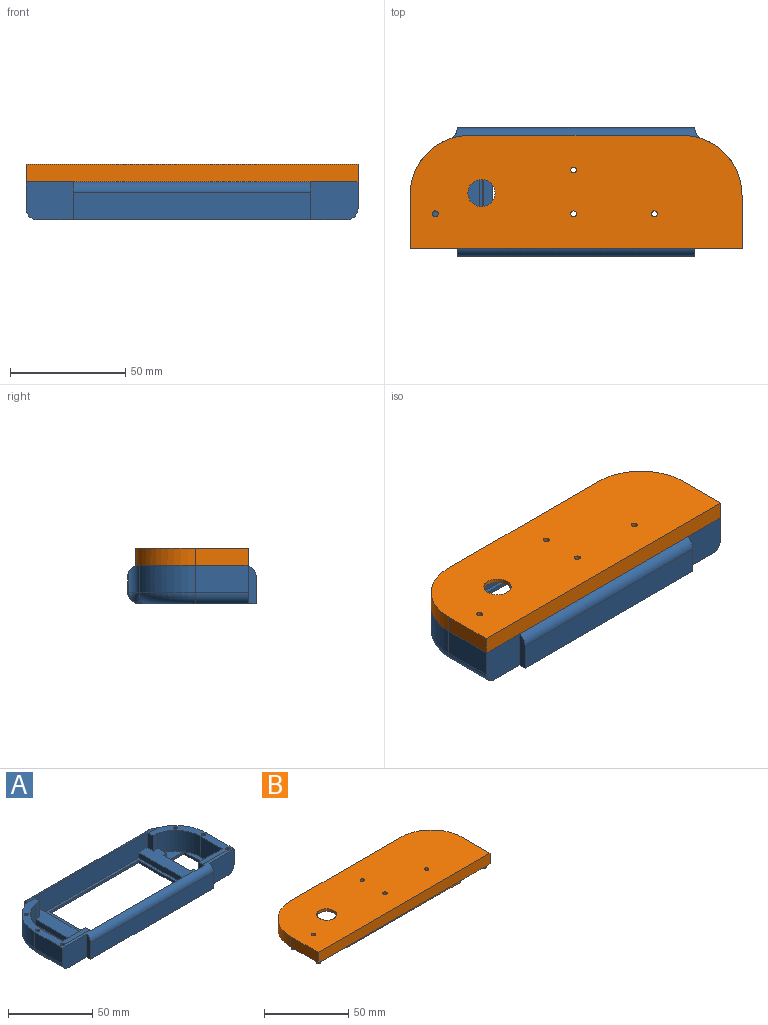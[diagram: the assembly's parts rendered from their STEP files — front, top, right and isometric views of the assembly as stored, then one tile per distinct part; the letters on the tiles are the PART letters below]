
ASSEMBLY  parts=2 mates=1
PART A: 89 faces, bbox 148.3x55.8x16.8 mm
  f0: plane 1.02x0.5mm, normal (0,-1,0), area 0.3mm2, adj f34,f35,f36
  f1: plane 47.75x9.68mm, normal (0,0,1), area 419.8mm2, adj f4,f6,f16,f28,f29,f39,f79,f83
  f2: plane 74.71x1.75mm, normal (0,1,0), area 130.7mm2, adj f12,f42,f43,f80
  f3: plane 74.71x1.75mm, normal (0,-1,0), area 130.7mm2, adj f12,f42,f43,f80
  f4: plane 38.27x4mm, normal (-1,0,0), area 153.1mm2, adj f1,f15,f16,f48
  f5: plane 45.75x24.5mm, normal (0,0,1), area 329.7mm2, adj f6,f15,f16,f17,f22,f23,f39,f55
  f6: plane 11x5.11mm, normal (1,0,0), area 56.2mm2, adj f1,f5,f29,f77,f79
  f7: plane 45.75x24.5mm, normal (0,0,1), area 329.7mm2, adj f14,f18,f19,f20,f41,f44,f45,f49
  f8: plane 8.13x4mm, normal (1,0,0), area 32.5mm2, adj f19,f40,f47,f52
  f9: plane 18.75x1.75mm, normal (1,0,0), area 32.8mm2, adj f10,f11,f12,f47
  f10: plane 13.13x1.75mm, normal (0,-1,0), area 23mm2, adj f9,f12,f47,f50
  f11: plane 13.13x1.75mm, normal (0,1,0), area 23mm2, adj f9,f12,f47,f50
  f12: plane 134x50.75mm, normal (0,0,-1), area 2811.7mm2, adj f2,f3,f9,f10,f11,f21,f24,f26
  f13: plane 7.39x4mm, normal (1,0,0), area 29.6mm2, adj f18,f40,f47,f53
  f14: plane 11x5.11mm, normal (-1,0,0), area 56.2mm2, adj f7,f29,f40,f49,f77
  f15: cylinder r=21mm len=20.27mm, axis (0,0,1), area 411.3mm2, adj f4,f5,f17,f48,f79
  f16: plane 19.5x15mm, normal (0,1,0), area 276.5mm2, adj f1,f4,f5,f17,f39,f48
  f17: plane 18x15mm, normal (1,0,0), area 270mm2, adj f5,f15,f16,f48
  f18: cylinder r=21mm len=20.27mm, axis (0,0,1), area 411.3mm2, adj f7,f13,f20,f47,f49
  f19: plane 19.5x15mm, normal (0,1,0), area 276.5mm2, adj f7,f8,f20,f40,f41,f47
  f20: plane 18x15mm, normal (-1,0,0), area 270mm2, adj f7,f18,f19,f47
  f21: plane 20.5x16.48mm, normal (0,-1,0), area 332.4mm2, adj f12,f23,f24,f67,f78
  f22: cylinder r=26mm len=24.46mm, axis (0,0,1), area 374.3mm2, adj f5,f23,f66,f73,f77
  f23: plane 23x11.75mm, normal (-1,0,0), area 270.1mm2, adj f5,f21,f22,f67,f78
  f24: plane 16.48x3.38mm, normal (-1,0,0), area 51.3mm2, adj f12,f21,f30,f78
  f25: plane 8.18x0.21mm, normal (1,0,0), area 1.6mm2, adj f32,f72,f75,f77
  f26: plane 16.48x3.38mm, normal (1,0,0), area 51.3mm2, adj f12,f30,f46,f78
  f27: plane 47.75x4mm, normal (-1,0,0), area 191mm2, adj f28,f29,f40,f43
  f28: plane 95x14.9mm, normal (0,1,0), area 1363.5mm2, adj f1,f27,f33,f35,f38,f39,f40,f41
  f29: plane 95x14.9mm, normal (0,-1,0), area 1363.5mm2, adj f1,f6,f14,f27,f34,f35,f36,f40
  f30: plane 103x11.75mm, normal (0,-1,0), area 1210.2mm2, adj f12,f24,f26,f78
  f31: plane 8.18x0.21mm, normal (-1,0,0), area 1.6mm2, adj f32,f70,f73,f77
  f32: plane 103x6.75mm, normal (0,1,0), area 695.2mm2, adj f25,f31,f71,f77
  f33: plane 6x1.45mm, normal (0,0,1), area 8.7mm2, adj f28,f37,f38,f82,f88
  f34: plane 35.75x1.45mm, normal (0,0,1), area 51.8mm2, adj f0,f29,f36,f81,f83
  f35: cylinder r=1.5mm len=47.75mm, axis (0,-1,0), area 18.3mm2, adj f0,f28,f29,f36,f37,f38,f43,f81
  f36: plane 35.75x0.5mm, normal (1,0,0), area 17.8mm2, adj f0,f29,f34,f35
  f37: plane 1.02x0.5mm, normal (0,1,0), area 0.3mm2, adj f33,f35,f38
  f38: plane 6x0.5mm, normal (1,0,0), area 3mm2, adj f28,f33,f35,f37
  f39: plane 11x4.38mm, normal (1,0,0), area 48.1mm2, adj f1,f5,f16,f28,f78
  f40: plane 47.75x11.13mm, normal (0,0,1), area 430.6mm2, adj f8,f13,f14,f19,f27,f28,f29,f41
  f41: plane 11x4.38mm, normal (-1,0,0), area 48.1mm2, adj f7,f19,f28,f40,f78
  f42: plane 44.31x1.75mm, normal (-1,0,0), area 77.5mm2, adj f2,f3,f12,f43
  f43: plane 80.65x47.75mm, normal (0,0,1), area 540.6mm2, adj f2,f3,f27,f28,f29,f35,f42,f80
  f44: cylinder r=26mm len=24.46mm, axis (0,0,1), area 374.3mm2, adj f7,f45,f68,f75,f77
  f45: plane 23x11.75mm, normal (1,0,0), area 270.1mm2, adj f7,f44,f46,f69,f78
  f46: plane 20.5x16.48mm, normal (0,-1,0), area 332.4mm2, adj f12,f26,f45,f69,f78
  f47: plane 38.27x18.26mm, normal (0,0,1), area 327.8mm2, adj f8,f9,f10,f11,f13,f18,f19,f20
  f48: plane 38.27x15.5mm, normal (0,0,1), area 511.2mm2, adj f4,f15,f16,f17
  f49: plane 11x4mm, normal (0,-1,0), area 44mm2, adj f7,f14,f18,f40
  f50: plane 18.75x1.75mm, normal (-1,0,0), area 32.8mm2, adj f10,f11,f12,f47
  f51: plane 22.75x4mm, normal (1,0,0), area 91mm2, adj f40,f47,f52,f53
  f52: plane 4x2.76mm, normal (0,1,0), area 11mm2, adj f8,f40,f47,f51
  f53: plane 4x2.76mm, normal (0,-1,0), area 11mm2, adj f13,f40,f47,f51
  f54: plane 2.5x2.5mm, normal (0,0,1), area 4.9mm2, adj f55
  f55: cylinder r=1.25mm len=2.5mm, axis (0,0,1), area 19.6mm2, adj f5,f54
  f56: plane 2.5x2.5mm, normal (0,0,1), area 4.9mm2, adj f57
  f57: cylinder r=1.25mm len=2.5mm, axis (0,0,1), area 19.6mm2, adj f7,f56,f78
  f58: plane 2.5x2.5mm, normal (0,0,1), area 4.9mm2, adj f59
  f59: cylinder r=1.25mm len=2.5mm, axis (0,0,1), area 19.6mm2, adj f7,f58
  f60: plane 2.5x2.5mm, normal (0,0,1), area 4.9mm2, adj f61
  f61: cylinder r=1.25mm len=2.5mm, axis (0,0,1), area 19.6mm2, adj f7,f60
  f62: plane 2.5x2.5mm, normal (0,0,1), area 4.9mm2, adj f63
  f63: cylinder r=1.25mm len=2.5mm, axis (0,0,1), area 19.6mm2, adj f5,f62,f78
  f64: cylinder r=1.25mm len=2.5mm, axis (0,0,1), area 19.6mm2, adj f5,f65
  f65: plane 2.5x2.5mm, normal (0,0,1), area 4.9mm2, adj f64
  f66: torus R=21mm, axis (0,0,-1), area 250.9mm2, adj f12,f22,f67,f74
  f67: cylinder r=5mm len=23mm, axis (0,-1,0), area 180.6mm2, adj f12,f21,f23,f66
  f68: torus R=21mm, axis (0,0,-1), area 250.9mm2, adj f12,f44,f69,f76
  f69: cylinder r=5mm len=23mm, axis (0,1,0), area 180.6mm2, adj f12,f45,f46,f68
  f70: cylinder r=5mm len=8.38mm, axis (0,1,0), area 9.3mm2, adj f12,f31,f71,f74
  f71: cylinder r=5mm len=103mm, axis (1,0,0), area 780.4mm2, adj f12,f32,f70,f72
  f72: cylinder r=5mm len=8.38mm, axis (0,-1,0), area 9.3mm2, adj f12,f25,f71,f76
  f73: cylinder r=5mm len=11.75mm, axis (0,0,1), area 67.2mm2, adj f22,f31,f74,f77
  f74: bspline ~8.31x8.18mm, area 36.4mm2, adj f66,f70,f73
  f75: cylinder r=5mm len=11.75mm, axis (0,0,1), area 67.2mm2, adj f25,f44,f76,f77
  f76: bspline ~8.31x8.18mm, area 36.4mm2, adj f68,f72,f75
  f77: cylinder r=5mm len=110.1mm, axis (-1,0,0), area 722.8mm2, adj f5,f6,f7,f14,f22,f25,f29,f31
  f78: cylinder r=5mm len=144mm, axis (1,0,0), area 780.2mm2, adj f5,f7,f21,f23,f24,f26,f28,f30
  f79: plane 11x4mm, normal (0,-1,0), area 44mm2, adj f1,f5,f6,f15
  f80: plane 44.31x1.75mm, normal (1,0,0), area 77.5mm2, adj f2,f3,f12,f43
  f81: plane 1x0.43mm, normal (0,1,0), area 0.2mm2, adj f34,f35,f83,f86
  f82: plane 1x0.43mm, normal (0,-1,0), area 0.2mm2, adj f33,f35,f86,f88
  f83: plane 35.75x3.5mm, normal (1,0,0), area 125.1mm2, adj f1,f29,f34,f81,f84
  f84: plane 2.5x0.7mm, normal (0,-1,0), area 1.7mm2, adj f1,f83,f86,f87
  f85: plane 2.5x0.7mm, normal (0,1,0), area 1.7mm2, adj f1,f86,f87,f88
  f86: plane 6x0.75mm, normal (0,0,1), area 4.5mm2, adj f35,f81,f82,f84,f85,f87
  f87: plane 6x2.5mm, normal (1,0,0), area 15mm2, adj f1,f84,f85,f86
  f88: plane 6x3.5mm, normal (1,0,0), area 21mm2, adj f1,f28,f33,f82,f85
PART B: 57 faces, bbox 144x49x10 mm
  f0: plane 23x7.77mm, normal (-1,0,0), area 172.6mm2, adj f2,f6,f7,f41,f44
  f1: plane 131x36mm, normal (0,0,-1), area 4203.9mm2, adj f8,f9,f10,f11,f12,f13,f14,f15
  f2: plane 144x7.77mm, normal (0,-1,0), area 1119.1mm2, adj f0,f3,f7,f44
  f3: plane 23x7.77mm, normal (1,0,0), area 172.6mm2, adj f2,f4,f7,f42,f44
  f4: cylinder r=26mm len=26mm, axis (0,0,-1), area 307.6mm2, adj f3,f5,f7,f42,f43
  f5: plane 92x7.77mm, normal (0,1,0), area 715mm2, adj f4,f6,f7,f43
  f6: cylinder r=26mm len=26mm, axis (0,0,-1), area 307.6mm2, adj f0,f5,f7,f41,f43
  f7: plane 144x49mm, normal (0,0,1), area 6637.8mm2, adj f0,f2,f3,f4,f5,f6,f13,f14
  f8: plane 9.75x5.63mm, normal (0.5,0.87,0), area 7.9mm2, adj f1,f9,f16,f19
  f9: plane 11.26x0.7mm, normal (1,0,0), area 7.9mm2, adj f1,f8,f10,f19
  f10: plane 9.75x5.63mm, normal (0.5,-0.87,0), area 7.9mm2, adj f1,f9,f11,f19
  f11: plane 9.75x5.63mm, normal (-0.5,-0.87,0), area 7.9mm2, adj f1,f10,f12,f19
  f12: plane 11.26x0.7mm, normal (-1,0,0), area 7.9mm2, adj f1,f11,f16,f19
  f13: cylinder r=1.25mm len=2.5mm, axis (0,0,1), area 19.6mm2, adj f1,f7
  f14: cylinder r=1.25mm len=2.5mm, axis (0,0,1), area 19.6mm2, adj f1,f7
  f15: cylinder r=1.25mm len=2.5mm, axis (0,0,1), area 19.6mm2, adj f1,f7
  f16: plane 9.75x5.63mm, normal (-0.5,0.87,0), area 7.9mm2, adj f1,f8,f12,f19
  f17: cylinder r=1.25mm len=2.5mm, axis (0,0,1), area 19.6mm2, adj f1,f7
  f18: cylinder r=5.88mm len=11.75mm, axis (0,0,1), area 66.4mm2, adj f7,f19
  f19: plane 22.52x19.5mm, normal (0,0,-1), area 220.9mm2, adj f8,f9,f10,f11,f12,f16,f18
  f20: plane 16.5x6.75mm, normal (1,0,0), area 111.4mm2, adj f1,f21,f25,f26
  f21: cylinder r=19.5mm len=19.5mm, axis (0,0,1), area 206.8mm2, adj f1,f20,f22,f26
  f22: plane 92x6.75mm, normal (0,-1,0), area 621mm2, adj f1,f21,f23,f26
  f23: cylinder r=19.5mm len=19.5mm, axis (0,0,1), area 206.8mm2, adj f1,f22,f24,f26
  f24: plane 16.5x6.75mm, normal (-1,0,0), area 111.4mm2, adj f1,f23,f25,f26
  f25: plane 131x6.75mm, normal (0,1,0), area 884.2mm2, adj f1,f20,f24,f26
  f26: plane 134x47.75mm, normal (0,0,-1), area 1312mm2, adj f20,f21,f22,f23,f24,f25,f27,f28
  f27: plane 5.11x1.75mm, normal (-1,0,0), area 8.9mm2, adj f26,f36,f40,f41,f43
  f28: plane 5.11x1.75mm, normal (1,0,0), area 8.9mm2, adj f26,f36,f39,f42,f43
  f29: cylinder r=21mm len=20.27mm, axis (0,0,1), area 48mm2, adj f26,f31,f40,f41
  f30: plane 19.5x1.75mm, normal (0,-1,0), area 34.1mm2, adj f26,f31,f37,f41
  f31: plane 18x1.75mm, normal (-1,0,0), area 31.5mm2, adj f26,f29,f30,f41
  f32: cylinder r=21mm len=20.27mm, axis (0,0,1), area 48mm2, adj f26,f34,f39,f42
  f33: plane 19.5x1.75mm, normal (0,-1,0), area 34.1mm2, adj f26,f34,f38,f42
  f34: plane 18x1.75mm, normal (1,0,0), area 31.5mm2, adj f26,f32,f33,f42
  f35: plane 95x1.65mm, normal (0,-1,0), area 156.7mm2, adj f26,f37,f38,f44
  f36: plane 95x1.65mm, normal (0,1,0), area 156.7mm2, adj f26,f27,f28,f43
  f37: plane 4.38x1.75mm, normal (-1,0,0), area 7.6mm2, adj f26,f30,f35,f41,f44
  f38: plane 4.38x1.75mm, normal (1,0,0), area 7.6mm2, adj f26,f33,f35,f42,f44
  f39: plane 4x1.75mm, normal (0,1,0), area 7mm2, adj f26,f28,f32,f42
  f40: plane 4x1.75mm, normal (0,1,0), area 7mm2, adj f26,f27,f29,f41
  f41: plane 45.75x24.5mm, normal (0,0,-1), area 329.7mm2, adj f0,f6,f27,f29,f30,f31,f37,f40
  f42: plane 45.75x24.5mm, normal (0,0,-1), area 329.7mm2, adj f3,f4,f28,f32,f33,f34,f38,f39
  f43: cylinder r=5mm len=110.1mm, axis (-1,0,0), area 76.6mm2, adj f4,f5,f6,f27,f28,f36,f41,f42
  f44: cylinder r=5mm len=144mm, axis (1,0,0), area 141.8mm2, adj f0,f2,f3,f35,f37,f38,f41,f42
  f45: plane 2.5x2.5mm, normal (0,0,-1), area 4.9mm2, adj f46
  f46: cylinder r=1.25mm len=2.5mm, axis (0,0,1), area 19.6mm2, adj f41,f45
  f47: plane 2.5x2.5mm, normal (0,0,-1), area 4.9mm2, adj f48
  f48: cylinder r=1.25mm len=2.5mm, axis (0,0,1), area 19.6mm2, adj f41,f44,f47
  f49: plane 2.5x2.5mm, normal (0,0,-1), area 4.9mm2, adj f50
  f50: cylinder r=1.25mm len=2.5mm, axis (0,0,1), area 19.6mm2, adj f42,f49
  f51: plane 2.5x2.5mm, normal (0,0,-1), area 4.9mm2, adj f52
  f52: cylinder r=1.25mm len=2.5mm, axis (0,0,1), area 19.6mm2, adj f42,f51
  f53: plane 2.5x2.5mm, normal (0,0,-1), area 4.9mm2, adj f54
  f54: cylinder r=1.25mm len=2.5mm, axis (0,0,1), area 19.6mm2, adj f42,f44,f53
  f55: plane 2.5x2.5mm, normal (0,0,-1), area 4.9mm2, adj f56
  f56: cylinder r=1.25mm len=2.5mm, axis (0,0,1), area 19.6mm2, adj f41,f55
PLACE A t=(86.3,-0.57,-68.82)mm
PLACE B t=(86.3,-0.57,-66.32)mm
MATE parallel B.f48 <-> A.f63  axis (0,0,-1) through (16.8,-17.57,-61.82)mm
